# Revit family: IS_Conca_T3951_BIM_IT
name_source: partatom
category: Plumbing Fixtures
revit_build: Autodesk Revit 2017 (Build: 20160225_1515(x64)
units: mm (PartAtom-declared; Revit-internal decimal feet)

## family parameters
Always vertical = No
Cut with Voids When Loaded = No
OmniClass Number = 23.45.05.14.21.11
OmniClass Title = Bath/Shower Units
Part Type = Normal
Room Calculation Point = No
Round Connector Dimension = Use Diameter
Shared = No
Work Plane-Based = No

## types (6) — shared parameters
BIMobject category = Storage
BIMobject category code = sanitary-storage
BIMobject main category = Sanitary
BIMobject main category code = sanitary
Installation instructions = https://www.idealspec.co.uk
Maniglia = No
Manufacturer = Ideal Standard
NominalDepth = 373 mm  [stored 1.22375 ft]
NominalHeight = 539 mm
NominalWidth = 1200 mm
PiattoDoccia = No
Product group = Bathroom_Furniture
URL = https://www.ideal-standard.co.uk
Uniclass 2015 Code = Pr_40_30_78_03
Uniclass 2015 Name = Bathroom cabinets
zero-valued in all types: CostoDiSostituzione, DimensioneScarico, LunghezzaNominale, Nominal depth, Nominal height, SeatMaterial, SpessoreDelMateriale, SpilloverLivello, Weight Net (Kg)

## per-type parameters (varying)
- T3951Y1 - Conca BSN UN 120X37X55 2 DR  NOWTOP  WHMT - T3951 - Y1_MattWhite: AltezzaNominale=0 mm  [stored 0 ft]; Description=Vanity unit, 1200 x 372 x 550mm with top to be drilled, 2 external drawers. Equipped with push open technology and soft locks and  Matt white lacquered finish; LarghezzaNominale=0 mm  [stored 0 ft]; Model=T3950Y1; ProfonditaNominale=0 mm  [stored 0 ft]
- T3951Y2 - Conca BSN UN 120X37X55 2 DR  NOWTOP  WHMT - T3951 - Y2_MattAntracite: Accessori=https://www.idealstandard.it; Aiuto=https://www.idealstandard.it; AltezzaNominale=540 mm; Autore=Ideal Standard; Brand=https://www.idealstandard.it; Caratteristiche=Mobile sottolavabo, 1200 x 372 x 550mm senza piano da appoggio per l'abbinamento ai piani in gres porcellanato o alle mensole  con 2 cassetti esterni. Dotato di tecnologia push open e soft close. Cassetti in metallo. Finitura Antracite laccato opaco; CodiceABarre=8014140461401; CodiceArticolo=T3951Y2; Colore=Matt anthracite; Description=Vanity unit, 1200 x 372 x 550mm without countertop to combine with porcelain stoneware tops or shelves with 2 external drawers. Equipped with push open and soft close technology.  Anthracite matt lacquer finish; DescrizioneClassifcazioneUni2015=Bathroom cabinets; Desrizione=Mobile sottolavabo, 1200 x 372 x 550mm senza piano da appoggio per l'abbinamento ai piani in gres porcellanato o alle mensole  con 2 cassetti esterni. Dotato di tecnologia push open e soft close. Cassetti in metallo. Finitura Antracite laccato opaco; DurataGaranzia=2; DurataGaranziaProdotti=2; Finitura=Matt anthracite; Forma=Rettangolare; Garanzia=Garanzia Idealstandard; IfcEsportaCome=IfcFurnitureType; InformaziniGaranzia=https://www.idealstandard.it; InformazioniDiProdotto=http://www.idealstandard.it; InformazioniGaranzia=https://www.idealstandard.it; InstruzioniInstallazione=https://www.idealstandard.it; LarghezzaNominale=1202 mm; Materiale=Ceramics; Model=T3951Y2; ModelloDiRiferimento=T3951Y2; Nome=BathroomCabinets_Conca_T3951Y2_IdealStandard; NomeOggettoBim=ISI_IdealStandard_Bathroom Cabinets_Conca_T3951Y2; NumeroDiModello=T3951Y2; PesoNetto=41; Produttore=Ideal Standard; ProfonditaNominale=373 mm  [stored 1.22375 ft]; Revisione=1; RiferimentoClassificazioneUni2015=Pr_40_30_78_03; Spazio=Interno; Telefono=800 652 290; TipoEspotazioneIfc=Bathroom cabinets; UnitàDurata=Anno; UnitàDurataGaranzia=Anno; UnitàLineare=Milimitre; UnitàMonetaria=€; UnitàSuperficie=Milimitre; UnitàVolume=Litri; Versione=1; VersioneClassificazioneUni2015=v1.1
- T3951Y3 - Conca BSN UN 120X37X55 2 DR  NOWTOP  WHMT - T3951 - Y3_MattSunset: Accessori=https://www.idealstandard.it; Aiuto=https://www.idealstandard.it; AltezzaNominale=540 mm; Autore=Ideal Standard; Brand=https://www.idealstandard.it; Caratteristiche=Mobile sottolavabo, 1200 x 372 x 550mm senza piano da appoggio per l'abbinamento ai piani in gres porcellanato o alle mensole  con 2 cassetti esterni. Dotato di tecnologia push open e soft close. Cassetti in metallo. Finitura Sunset laccato opaco; CodiceABarre=8014140461418; CodiceArticolo=T3951Y3; Colore=Matt Sunset; Description=Vanity unit, 1200 x 372 x 550mm without countertop to combine with porcelain stoneware tops or shelves with 2 external drawers. Equipped with push open and soft close technology.  Sunset matt lacquer finish; DescrizioneClassifcazioneUni2015=Bathroom cabinets; Desrizione=Mobile sottolavabo, 1200 x 372 x 550mm senza piano da appoggio per l'abbinamento ai piani in gres porcellanato o alle mensole  con 2 cassetti esterni. Dotato di tecnologia push open e soft close. Cassetti in metallo. Finitura Sunset laccato opaco; DurataGaranzia=2; DurataGaranziaProdotti=2; Finitura=Matt Sunset; Forma=Rettangolare; Garanzia=Garanzia Idealstandard; IfcEsportaCome=IfcFurnitureType; InformaziniGaranzia=https://www.idealstandard.it; InformazioniDiProdotto=http://www.idealstandard.it; InformazioniGaranzia=https://www.idealstandard.it; InstruzioniInstallazione=https://www.idealstandard.it; LarghezzaNominale=1202 mm; Materiale=Ceramics; Model=T3951Y3; ModelloDiRiferimento=T3951Y3; Nome=BathroomCabinets_Conca_T3951Y3_IdealStandard; NomeOggettoBim=ISI_IdealStandard_Bathroom Cabinets_Conca_T3951Y3; NumeroDiModello=T3951Y3; PesoNetto=41; Produttore=Ideal Standard; ProfonditaNominale=373 mm  [stored 1.22375 ft]; Revisione=1; RiferimentoClassificazioneUni2015=Pr_40_30_78_03; Spazio=Interno; Telefono=800 652 290; TipoEspotazioneIfc=Bathroom cabinets; UnitàDurata=Anno; UnitàDurataGaranzia=Anno; UnitàLineare=Milimitre; UnitàMonetaria=€; UnitàSuperficie=Milimitre; UnitàVolume=Litri; Versione=1; VersioneClassificazioneUni2015=v1.1
- T3951Y4 - Conca BSN UN 120X37X55 2 DR  NOWTOP  WHMT - T3951 - Y4_SmokedOak: Accessori=https://www.idealstandard.it; Aiuto=https://www.idealstandard.it; AltezzaNominale=540 mm; Autore=Ideal Standard; Brand=https://www.idealstandard.it; Caratteristiche=Mobile sottolavabo, 1200 x 372 x 550mm senza piano da appoggio per l'abbinamento ai piani in gres porcellanato o alle mensole  con 2 cassetti esterni. Dotato di tecnologia push open e soft close. Cassetti in metallo. Finitura Rovere affumicato scuro; CodiceABarre=8014140461425; CodiceArticolo=T3951Y4; Colore=Smoked Oak; Description=Vanity unit, 1200 x 372 x 550mm without countertop to combine with porcelain stoneware tops or shelves with 2 external drawers. Equipped with push open and soft close technology.  Dark smoked oak finish; DescrizioneClassifcazioneUni2015=Bathroom cabinets; Desrizione=Mobile sottolavabo, 1200 x 372 x 550mm senza piano da appoggio per l'abbinamento ai piani in gres porcellanato o alle mensole  con 2 cassetti esterni. Dotato di tecnologia push open e soft close. Cassetti in metallo. Finitura Rovere affumicato scuro; DurataGaranzia=2; DurataGaranziaProdotti=2; Finitura=Smoked Oak; Forma=Rettangolare; Garanzia=Garanzia Idealstandard; IfcEsportaCome=IfcFurnitureType; InformaziniGaranzia=https://www.idealstandard.it; InformazioniDiProdotto=http://www.idealstandard.it; InformazioniGaranzia=https://www.idealstandard.it; InstruzioniInstallazione=https://www.idealstandard.it; LarghezzaNominale=1202 mm; Materiale=Ceramics; Model=T3951Y4; ModelloDiRiferimento=T3951Y4; Nome=BathroomCabinets_Conca_T3951Y4_IdealStandard; NomeOggettoBim=ISI_IdealStandard_Bathroom Cabinets_Conca_T3951Y4; NumeroDiModello=T3951Y4; PesoNetto=41; Produttore=Ideal Standard; ProfonditaNominale=373 mm  [stored 1.22375 ft]; Revisione=1; RiferimentoClassificazioneUni2015=Pr_40_30_78_03; Spazio=Interno; Telefono=800 652 290; TipoEspotazioneIfc=Bathroom cabinets; UnitàDurata=Anno; UnitàDurataGaranzia=Anno; UnitàLineare=Milimitre; UnitàMonetaria=€; UnitàSuperficie=Milimitre; UnitàVolume=Litri; Versione=1; VersioneClassificazioneUni2015=v1.1
- T3951Y5 - Conca BSN UN 120X37X55 2 DR  NOWTOP  WHMT - T3951 - Y5_DarkWalnut: Accessori=https://www.idealstandard.it; Aiuto=https://www.idealstandard.it; AltezzaNominale=540 mm; Autore=Ideal Standard; Brand=https://www.idealstandard.it; Caratteristiche=Mobile sottolavabo, 1200 x 372 x 550mm senza piano da appoggio per l'abbinamento ai piani in gres porcellanato o alle mensole  con 2 cassetti esterni. Dotato di tecnologia push open e soft close. Cassetti in metallo. Finitura Noce scuro; CodiceABarre=8014140461432; CodiceArticolo=T3951Y5; Colore=Dark Walnut; Description=Vanity unit, 1200 x 372 x 550mm without countertop to combine with porcelain stoneware tops or shelves with 2 external drawers. Equipped with push open and soft close technology.  Dark Walnut finish; DescrizioneClassifcazioneUni2015=Bathroom cabinets; Desrizione=Mobile sottolavabo, 1200 x 372 x 550mm senza piano da appoggio per l'abbinamento ai piani in gres porcellanato o alle mensole  con 2 cassetti esterni. Dotato di tecnologia push open e soft close. Cassetti in metallo. Finitura Noce scuro; DurataGaranzia=2; DurataGaranziaProdotti=2; Finitura=Dark Walnut; Forma=Rettangolare; Garanzia=Garanzia Idealstandard; IfcEsportaCome=IfcFurnitureType; InformaziniGaranzia=https://www.idealstandard.it; InformazioniDiProdotto=http://www.idealstandard.it; InformazioniGaranzia=https://www.idealstandard.it; InstruzioniInstallazione=https://www.idealstandard.it; LarghezzaNominale=1202 mm; Materiale=Ceramics; Model=T3951Y5; ModelloDiRiferimento=T3951Y5; Nome=BathroomCabinets_Conca_T3951Y5_IdealStandard; NomeOggettoBim=ISI_IdealStandard_Bathroom Cabinets_Conca_T3951Y5; NumeroDiModello=T3951Y5; PesoNetto=41; Produttore=Ideal Standard; ProfonditaNominale=373 mm  [stored 1.22375 ft]; Revisione=1; RiferimentoClassificazioneUni2015=Pr_40_30_78_03; Spazio=Interno; Telefono=800 652 290; TipoEspotazioneIfc=Bathroom cabinets; UnitàDurata=Anno; UnitàDurataGaranzia=Anno; UnitàLineare=Milimitre; UnitàMonetaria=€; UnitàSuperficie=Milimitre; UnitàVolume=Litri; Versione=1; VersioneClassificazioneUni2015=v1.1
- T3951Y6 - Conca BSN UN 120X37X55 2 DR  NOWTOP  WHMT - T3951 - Y6_LightOak: Accessori=https://www.idealstandard.it; Aiuto=https://www.idealstandard.it; AltezzaNominale=540 mm; Autore=Ideal Standard; Brand=https://www.idealstandard.it; Caratteristiche=Mobile sottolavabo, 1200 x 372 x 550mm senza piano da appoggio per l'abbinamento ai piani in gres porcellanato o alle mensole  con 2 cassetti esterni. Dotato di tecnologia push open e soft close. Cassetti in metallo. Finitura Legno chiaro; CodiceABarre=8014140461449; CodiceArticolo=T3951Y6; Colore=Light Oak; Description=Vanity unit, 1200 x 372 x 550mm without countertop to combine with porcelain stoneware tops or shelves with 2 external drawers. Equipped with push open and soft close technology.  Light wood finish; DescrizioneClassifcazioneUni2015=Bathroom cabinets; Desrizione=Mobile sottolavabo, 1200 x 372 x 550mm senza piano da appoggio per l'abbinamento ai piani in gres porcellanato o alle mensole  con 2 cassetti esterni. Dotato di tecnologia push open e soft close. Cassetti in metallo. Finitura Legno chiaro; DurataGaranzia=2; DurataGaranziaProdotti=2; Finitura=Light Oak; Forma=Rettangolare; Garanzia=Garanzia Idealstandard; IfcEsportaCome=IfcFurnitureType; InformaziniGaranzia=https://www.idealstandard.it; InformazioniDiProdotto=http://www.idealstandard.it; InformazioniGaranzia=https://www.idealstandard.it; InstruzioniInstallazione=https://www.idealstandard.it; LarghezzaNominale=1202 mm; Materiale=Ceramics; Model=T3951Y6; ModelloDiRiferimento=T3951Y6; Nome=BathroomCabinets_Conca_T3951Y6_IdealStandard; NomeOggettoBim=ISI_IdealStandard_Bathroom Cabinets_Conca_T3951Y6; NumeroDiModello=T3951Y6; PesoNetto=41; Produttore=Ideal Standard; ProfonditaNominale=373 mm  [stored 1.22375 ft]; Revisione=1; RiferimentoClassificazioneUni2015=Pr_40_30_78_03; Spazio=Interno; Telefono=800 652 290; TipoEspotazioneIfc=Bathroom cabinets; UnitàDurata=Anno; UnitàDurataGaranzia=Anno; UnitàLineare=Milimitre; UnitàMonetaria=€; UnitàSuperficie=Milimitre; UnitàVolume=Litri; Versione=1; VersioneClassificazioneUni2015=v1.1

note: [stored X ft] marks values corroborated as IEEE doubles in the binary element streams (Revit-internal decimal feet)

## geometry (parser evidence)
native form markers: Sweep x3
no freeform markers — native parametric forms only
